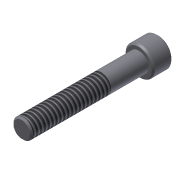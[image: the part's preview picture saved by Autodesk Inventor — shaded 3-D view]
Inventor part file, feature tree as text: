
AUTODESK INVENTOR PART (.ipt)
format: ipt  version: 2011 (Build 150239000, 239)  size: 104,448 bytes
history: native  units: in
note: dims shown in document units (in); Inventor stores cm internally (conversion verified against a paired STEP export)
features: extrude x3, sketch x3, chamfer x1, thread x1
ambient origin geometry x8: Origin, YZ Plane, XZ Plane, XY Plane, X Axis, Y Axis, Z Axis, Center Point
bodies: Solid1 (feature_tree)
feature tree (8):
  extrude  "Extrusion1"  Depth=1.5in TaperAngle=0.0deg
  extrude  "Extrusion2"  Depth=0.25in TaperAngle=0.0deg
  extrude  "Extrusion3"  Depth=0.125in TaperAngle=0.0deg
  chamfer  "Chamfer1"  Distance=0.02in Angle=45.0deg
  thread  "Thread1"  [1 undecoded]
  sketch  "Sketch1"  dims[d0=0.25in d1=1.5in d2=0.0in]
  sketch  "Sketch2"  dims[d3=0.375in d4=0.25in d5=0.0in]
  sketch  "Sketch3"  dims[d6=0.1875in d7=0.125in d8=0.0in d9=0.02in d10=0.125in d11=45.0deg d12=1.0in d13=0.0in]
note: 1 required parameter value undecoded (feature->parameter linkage not recoverable at this tier; creation-order binding heuristic only, values carry confidence <= 0.55)
